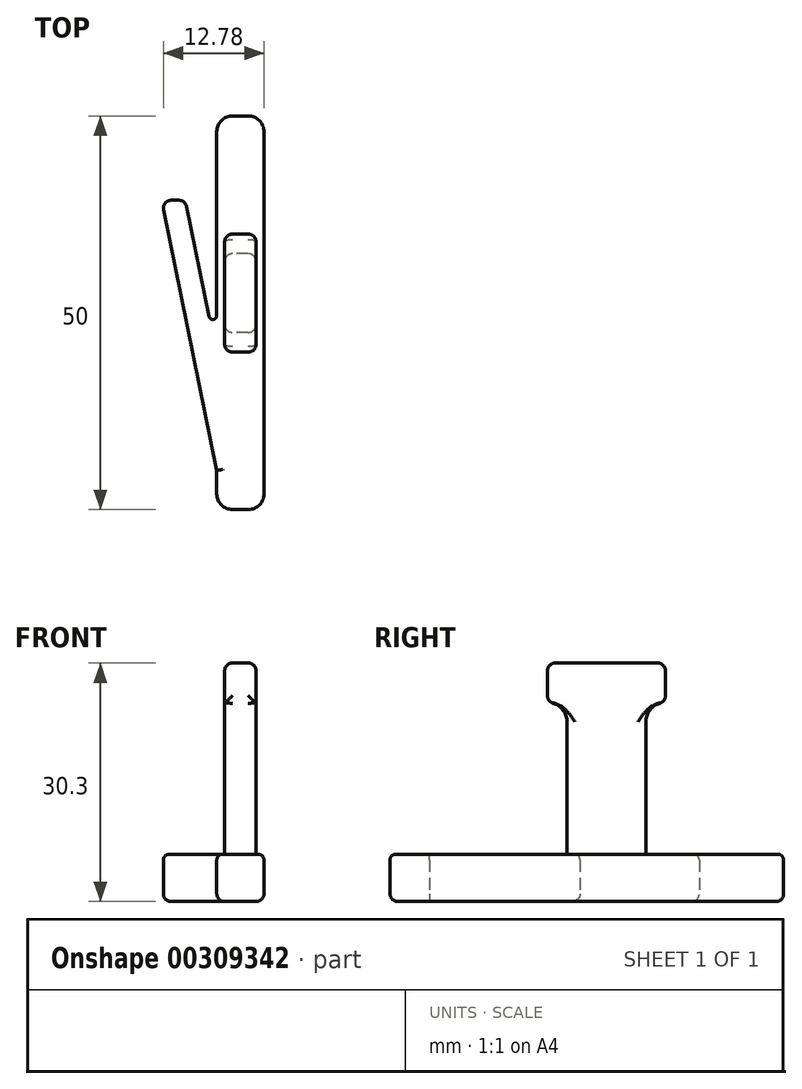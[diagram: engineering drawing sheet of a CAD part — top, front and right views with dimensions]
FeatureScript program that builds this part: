
annotation { "Feature Type Name" : "Feature", "Feature Type Description" : "" }
export const myFeature = defineFeature(function(context is Context, id is Id, definition is map)
    precondition{}
    {
        {
            var Q0;
            Q0=qCreatedBy(makeId("Top.planeOp"),FACE);
            var sketch = newSketch(context, id + "F0", { "sketchPlane" : qUnion([Q0])});
            skLineSegment(sketch, "E0.bottom", {"start": v(0, 0) * mm, "end": v(6, 0) * mm});
            skLineSegment(sketch, "E0.top", {"start": v(0, -50) * mm, "end": v(6, -50) * mm});
            skLineSegment(sketch, "E0.left", {"start": v(0, 0) * mm, "end": v(0, -50) * mm});
            skLineSegment(sketch, "E0.right", {"start": v(6, 0) * mm, "end": v(6, -50) * mm});
            skLineSegment(sketch, "E1", {"start": v(0, -50) * mm, "end": v(0, -45) * mm});
            skLineSegment(sketch, "E2", {"start": v(0, -45) * mm, "end": v(-7, -45) * mm});
            skLineSegment(sketch, "E3", {"start": v(0, -45) * mm, "end": v(-7, -10.7) * mm});
            skLineSegment(sketch, "E4", {"start": v(-7, -10.7) * mm, "end": v(-4, -10.7) * mm});
            skLineSegment(sketch, "E5", {"start": v(-4, -10.7) * mm, "end": v(0, -30.3) * mm});
            skSolve(sketch);
        }
        {
            var Q0;
            Q0=qSketchRegion(id+"F0",true);
            extrude(context, id + "F1", {"entities" : qUnion([Q0]), "depth" : 6 * mm});
        }
        {
            var Q0;
            Q0=makeQuery(id+"F1.opExtrude","SWEPT_EDGE",EDGE,{"disambiguationData":[OSD([sQuery(id+"F0.wireOp",EDGE,"E3"),sQuery(id+"F0.wireOp",EDGE,"E4")])]});
            var Q1;
            Q1=makeQuery(id+"F1.opExtrude","SWEPT_EDGE",EDGE,{"disambiguationData":[OSD([sQuery(id+"F0.wireOp",EDGE,"E4"),sQuery(id+"F0.wireOp",EDGE,"E5")])]});
            fillet(context, id + "F2", {"entities" : qUnion([Q0, Q1]), "radius" : 1 * mm, "tangentPropagation" : true, "allowEdgeOverflow" : false});
        }
        {
            var Q0;
            Q0=makeQuery(id+"F1.opExtrude","SWEPT_EDGE",EDGE,{"disambiguationData":[OSD([sQuery(id+"F0.wireOp",EDGE,"E0.left"),sQuery(id+"F0.wireOp",EDGE,"E5")])]});
            fillet(context, id + "F3", {"entities" : qUnion([Q0]), "radius" : .5 * mm, "tangentPropagation" : true, "allowEdgeOverflow" : false});
        }
        {
            var Q0;
            Q0=makeQuery(id+"F1.opExtrude","SWEPT_EDGE",EDGE,{"disambiguationData":[OSD([sQuery(id+"F0.wireOp",EDGE,"E0.bottom"),sQuery(id+"F0.wireOp",EDGE,"E0.left")])]});
            var Q1;
            Q1=makeQuery(id+"F1.opExtrude","SWEPT_EDGE",EDGE,{"disambiguationData":[OSD([sQuery(id+"F0.wireOp",EDGE,"E0.bottom"),sQuery(id+"F0.wireOp",EDGE,"E0.right")])]});
            var Q2;
            Q2=makeQuery(id+"F1.opExtrude","SWEPT_EDGE",EDGE,{"disambiguationData":[OSD([sQuery(id+"F0.wireOp",EDGE,"E0.top"),sQuery(id+"F0.wireOp",EDGE,"E0.right")])]});
            var Q3;
            Q3=makeQuery(id+"F1.opExtrude","SWEPT_EDGE",EDGE,{"disambiguationData":[OSD([sQuery(id+"F0.wireOp",EDGE,"E0.top"),sQuery(id+"F0.wireOp",EDGE,"E1")])]});
            fillet(context, id + "F4", {"entities" : qUnion([Q0, Q1, Q2, Q3]), "radius" : 2 * mm, "tangentPropagation" : true, "allowEdgeOverflow" : false});
        }
        {
            var Q0;
            Q0=makeQuery(id+"F1.opExtrude","CAP_FACE",FACE,{"disambiguationData":[OSD([sQuery(id+"F0.wireOp",EDGE,"E0.bottom"),sQuery(id+"F0.wireOp",EDGE,"E0.top"),sQuery(id+"F0.wireOp",EDGE,"E0.left"),sQuery(id+"F0.wireOp",EDGE,"E0.right"),sQuery(id+"F0.wireOp",EDGE,"E1"),sQuery(id+"F0.wireOp",EDGE,"E3"),sQuery(id+"F0.wireOp",EDGE,"E4"),sQuery(id+"F0.wireOp",EDGE,"E5")])],"isStart":false});
            fillet(context, id + "F5", {"entities" : qUnion([Q0]), "radius" : .7 * mm, "allowEdgeOverflow" : false});
        }
        {
            var Q0;
            Q0=makeQuery(id+"F1.opExtrude","SWEPT_FACE",FACE,{"disambiguationData":[OSD([sQuery(id+"F0.wireOp",EDGE,"E0.right")])]});
            var sketch = newSketch(context, id + "F6", { "sketchPlane" : qUnion([Q0])});
            skLineSegment(sketch, "E6.bottom", {"start": v(-27.5, 5.76) * mm, "end": v(-17.5, 5.76) * mm});
            skLineSegment(sketch, "E6.top", {"start": v(-27.5, 25.76) * mm, "end": v(-17.5, 25.76) * mm});
            skLineSegment(sketch, "E6.left", {"start": v(-27.5, 5.76) * mm, "end": v(-27.5, 25.76) * mm});
            skLineSegment(sketch, "E6.right", {"start": v(-17.5, 5.76) * mm, "end": v(-17.5, 25.76) * mm});
            skLineSegment(sketch, "E7.bottom", {"start": v(-30, 25.3) * mm, "end": v(-15, 25.3) * mm});
            skLineSegment(sketch, "E7.top", {"start": v(-30, 30.3) * mm, "end": v(-15, 30.3) * mm});
            skLineSegment(sketch, "E7.left", {"start": v(-30, 25.3) * mm, "end": v(-30, 30.3) * mm});
            skLineSegment(sketch, "E7.right", {"start": v(-15, 25.3) * mm, "end": v(-15, 30.3) * mm});
            skLineSegment(sketch, "E8", {"start": v(-27.5, 5.76) * mm, "end": v(-27.5, 4.76) * mm});
            skLineSegment(sketch, "E9", {"start": v(-27.5, 4.76) * mm, "end": v(-17.5, 4.76) * mm});
            skLineSegment(sketch, "E10", {"start": v(-17.5, 4.76) * mm, "end": v(-17.5, 5.76) * mm});
            skSolve(sketch);
        }
        {
            var Q0;
            {var subQ1=sQuery(id+"F6.wireOp",EDGE,"E6.top");Q0=makeQuery(id+"F6.imprint","IMPRINT",FACE,{"disambiguationData":[TD([[makeQuery(id+"F6.imprint","IMPRINT",EDGE,{"derivedFrom":subQ1}),1.0]])]});}
            var Q1;
            {var subQ0=sQuery(id+"F6.wireOp",EDGE,"E6.bottom");Q1=makeQuery(id+"F6.imprint","IMPRINT",FACE,{"disambiguationData":[TD([[makeQuery(id+"F6.imprint","IMPRINT",EDGE,{"derivedFrom":subQ0}),1.0]])]});}
            var Q2;
            {var subQ0=sQuery(id+"F6.wireOp",EDGE,"E6.top");Q2=makeQuery(id+"F6.imprint","IMPRINT",FACE,{"disambiguationData":[TD([[makeQuery(id+"F6.imprint","IMPRINT",EDGE,{"derivedFrom":subQ0}),-1.0]])]});}
            extrude(context, id + "F7", {"entities" : qUnion([Q0, Q1, Q2]), "operationType" : NewBodyOperationType.ADD, "oppositeDirection" : true, "depth" : 5 * mm, "hasSecondDirection" : true, "secondDirectionOppositeDirection" : true, "secondDirectionDepth" : 1 * mm});
        }
        {
            var Q0;
            Q0=makeQuery(id+"F7.opExtrude","CAP_EDGE",EDGE,{"disambiguationData":[OSD([sQuery(id+"F6.wireOp",EDGE,"E6.right")])],"isStart":false});
            var Q1;
            Q1=makeQuery(id+"F7.opExtrude","CAP_EDGE",EDGE,{"disambiguationData":[OSD([sQuery(id+"F6.wireOp",EDGE,"E6.right")])],"isStart":true});
            var Q2;
            Q2=makeQuery(id+"F7.opExtrude","CAP_EDGE",EDGE,{"disambiguationData":[OSD([sQuery(id+"F6.wireOp",EDGE,"E6.left")])],"isStart":true});
            var Q3;
            Q3=makeQuery(id+"F7.opExtrude","CAP_EDGE",EDGE,{"disambiguationData":[OSD([sQuery(id+"F6.wireOp",EDGE,"E6.left")])],"isStart":false});
            var Q4;
            Q4=makeQuery(id+"F7.opExtrude","SWEPT_EDGE",EDGE,{"disambiguationData":[OSD([sQuery(id+"F6.wireOp",EDGE,"E7.top"),sQuery(id+"F6.wireOp",EDGE,"E7.right")])]});
            var Q5;
            Q5=makeQuery(id+"F7.opExtrude","SWEPT_EDGE",EDGE,{"disambiguationData":[OSD([sQuery(id+"F6.wireOp",EDGE,"E7.top"),sQuery(id+"F6.wireOp",EDGE,"E7.left")])]});
            fillet(context, id + "F8", {"entities" : qUnion([Q0, Q1, Q2, Q3, Q4, Q5]), "radius" : 1 * mm, "allowEdgeOverflow" : false});
        }
        {
            var Q0;
            Q0=makeQuery(id+"F7.opExtrude","SWEPT_EDGE",EDGE,{"disambiguationData":[OSD([sQuery(id+"F6.wireOp",EDGE,"E6.right"),sQuery(id+"F6.wireOp",EDGE,"E7.bottom")])]});
            var Q1;
            Q1=makeQuery(id+"F7.opExtrude","SWEPT_EDGE",EDGE,{"disambiguationData":[OSD([sQuery(id+"F6.wireOp",EDGE,"E6.left"),sQuery(id+"F6.wireOp",EDGE,"E7.bottom")])]});
            fillet(context, id + "F9", {"entities" : qUnion([Q0, Q1]), "radius" : 2.5 * mm, "tangentPropagation" : true, "allowEdgeOverflow" : false});
        }
        {
            var Q0;
            Q0=makeQuery(id+"F7.opExtrude","CAP_EDGE",EDGE,{"disambiguationData":[OSD([sQuery(id+"F6.wireOp",EDGE,"E7.top")])],"isStart":false});
            var Q1;
            Q1=makeQuery(id+"F7.opExtrude","CAP_EDGE",EDGE,{"disambiguationData":[OSD([sQuery(id+"F6.wireOp",EDGE,"E7.top")])],"isStart":true});
            var Q2;
            Q2=makeQuery(id+"F7.opExtrude","CAP_EDGE",EDGE,{"disambiguationData":[OSD([sQuery(id+"F6.wireOp",EDGE,"E7.right")])],"isStart":false});
            var Q3;
            Q3=makeQuery(id+"F7.opExtrude","CAP_EDGE",EDGE,{"disambiguationData":[OSD([sQuery(id+"F6.wireOp",EDGE,"E7.right")])],"isStart":true});
            var Q4;
            Q4=makeQuery(id+"F9.opFillet","BLEND_EDGE",EDGE,{"blendedFrom":[makeQuery(id+"F7.opExtrude","SWEPT_EDGE",EDGE,{"disambiguationData":[OSD([sQuery(id+"F6.wireOp",EDGE,"E6.right"),sQuery(id+"F6.wireOp",EDGE,"E7.bottom")])]}),makeQuery(id+"F7.opExtrude","SWEPT_FACE",FACE,{"disambiguationData":[OSD([sQuery(id+"F6.wireOp",EDGE,"E7.right")])]})],"blendedInto":[makeQuery(id+"F7.opExtrude","SWEPT_FACE",FACE,{"disambiguationData":[OSD([sQuery(id+"F6.wireOp",EDGE,"E7.right")])]})]});
            var Q5;
            Q5=makeQuery(id+"F7.opExtrude","CAP_EDGE",EDGE,{"disambiguationData":[OSD([sQuery(id+"F6.wireOp",EDGE,"E7.left")])],"isStart":false});
            var Q6;
            Q6=makeQuery(id+"F7.opExtrude","CAP_EDGE",EDGE,{"disambiguationData":[OSD([sQuery(id+"F6.wireOp",EDGE,"E7.left")])],"isStart":true});
            var Q7;
            Q7=makeQuery(id+"F9.opFillet","BLEND_EDGE",EDGE,{"blendedFrom":[makeQuery(id+"F7.opExtrude","SWEPT_EDGE",EDGE,{"disambiguationData":[OSD([sQuery(id+"F6.wireOp",EDGE,"E6.left"),sQuery(id+"F6.wireOp",EDGE,"E7.bottom")])]}),makeQuery(id+"F7.opExtrude","SWEPT_FACE",FACE,{"disambiguationData":[OSD([sQuery(id+"F6.wireOp",EDGE,"E7.left")])]})],"blendedInto":[makeQuery(id+"F7.opExtrude","SWEPT_FACE",FACE,{"disambiguationData":[OSD([sQuery(id+"F6.wireOp",EDGE,"E7.left")])]})]});
            fillet(context, id + "F10", {"entities" : qUnion([Q0, Q1, Q2, Q3, Q4, Q5, Q6, Q7]), "radius" : 1 * mm, "allowEdgeOverflow" : false});
        }
        {
            var Q0;
            Q0=makeQuery(id+"F1.opExtrude","CAP_FACE",FACE,{"disambiguationData":[OSD([sQuery(id+"F0.wireOp",EDGE,"E0.bottom"),sQuery(id+"F0.wireOp",EDGE,"E0.top"),sQuery(id+"F0.wireOp",EDGE,"E0.left"),sQuery(id+"F0.wireOp",EDGE,"E0.right"),sQuery(id+"F0.wireOp",EDGE,"E1"),sQuery(id+"F0.wireOp",EDGE,"E3"),sQuery(id+"F0.wireOp",EDGE,"E4"),sQuery(id+"F0.wireOp",EDGE,"E5")])],"isStart":true});
            fillet(context, id + "F11", {"entities" : qUnion([Q0]), "radius" : 1 * mm, "tangentPropagation" : true, "allowEdgeOverflow" : false});
        }
    });
